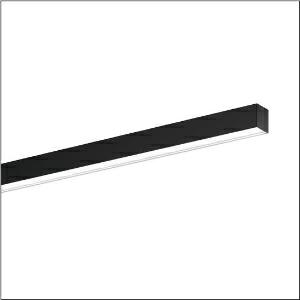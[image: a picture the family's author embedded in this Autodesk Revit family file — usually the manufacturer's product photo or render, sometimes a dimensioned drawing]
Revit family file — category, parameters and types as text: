
# Revit family: silica_21_51mx23db45bb
name_source: partatom
category: Lighting Fixtures
units: mm (PartAtom-declared; Revit-internal decimal feet)

## family parameters
Cut with Voids When Loaded = No
Host = Face
Light Source = No
Part Type = Normal
Room Calculation Point = No
Round Connector Dimension = Use Diameter
Shared = No

## types (1)
- --- (1 x LED, 4100 lm, 28.1 W, 4000K)
    Apparent Load = 28 VA
    CIE Flux Codes = 78 96 99 100 100
    Color Rendering = 80
    Color Temperature = 4000K
    Default Elevation = 1800 mm
    Description = Silica 21, office luminaire, primary optical cover: prismatic diffuser, of PMMA, CAT 2 (L<= 3000cd/m²), light emission: direct distribution, primary light characteristic: symmetric, installation type: surface-mounted, LED, rated luminous flux: 4.100lm, luminous efficacy: 146lm/W, light colour: 840, colour temperature: 4000K, control gear: DALI 2, with terminal, 3+2-pole, max. 2.5mm², mains connection: 220..240V, AC, 50/60Hz, rated input power: 28.1W, luminaire housing, of aluminium, matt jet black (RAL 9005), length: 1.504mm, width: 53mm, height: 53mm, protection rating (complete): IP20, insulation class (complete): insulation class I (protective earthing), certification: CE, permissible operating ambient temperature: 0..+35°C, standard: EN 50419, packaging unit: 1 piece
    Height = 53 mm
    Lamp = 1 x LED
    Lamp Light Flux = 4100 lm
    Lamp Power = 28.1 W
    Lamp count = 1
    Length = 1504 mm
    Luminous efficacy = 146 lm/W
    Manufacturer = Siteco
    ModVariant = No
    Model = 51MX23DB45BB
    Mounting Place = Ceiling
    Mounting Type = Surface mounted
    Number of Poles = 1
    OnlyDefault = Yes
    Power Factor = 1
    Product Name = Silica 21
    Product group = office luminaire | ceiling mounted
    ProductGroupID = 301
    Protection Class = Protection class I
    Protection Degree = IP 20
    RLX_Detail_Level = 1
    RLX_Emergency_Light_Flux = 0 lm
    RLX_Emergency_Type = 0
    RLX_Emergency_Type_DB = No
    RlxData = <blob elided: 23825 chars, md5=9fc26c3c>
    Socket = socket
    Standby Power = 0 W
    System Light Flux = 4100 lm
    System Power = 28 W
    Type Comments = factory setting: luminous flux: 100 % | dim-lin: 254 | 323 mA
    Type Image = l_1335925.jpg
    URL = http://relux.com
    VarID = @adj_121145
    Voltage = 0 V
    Weight = 0.00 kg
    Width = 53 mm

## geometry (parser evidence)
native form markers: Blend x4, Sweep x10
no freeform markers — native parametric forms only
